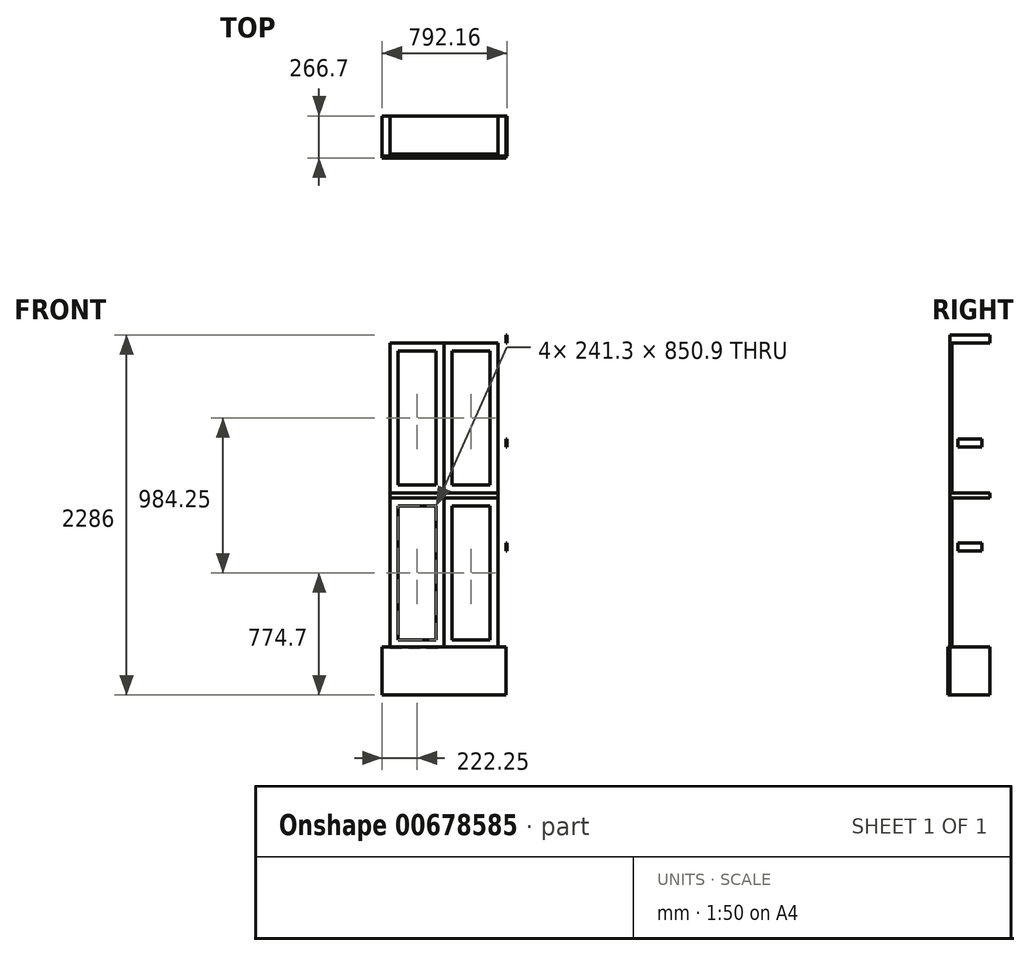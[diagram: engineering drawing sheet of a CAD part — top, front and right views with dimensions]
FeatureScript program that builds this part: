
annotation { "Feature Type Name" : "Feature", "Feature Type Description" : "" }
export const myFeature = defineFeature(function(context is Context, id is Id, definition is map)
    precondition{}
    {
        {
            var Q0;
            Q0=qCreatedBy(makeId("Front.planeOp"),FACE);
            var sketch = newSketch(context, id + "F0", { "sketchPlane" : qUnion([Q0])});
            skLineSegment(sketch, "E0.bottom", {"start": v(393.7, 152.4) * mm, "end": v(-393.7, 152.4) * mm});
            skLineSegment(sketch, "E0.top", {"start": v(393.7, -152.4) * mm, "end": v(-393.7, -152.4) * mm});
            skLineSegment(sketch, "E0.left", {"start": v(393.7, 152.4) * mm, "end": v(393.7, -152.4) * mm});
            skLineSegment(sketch, "E0.right", {"start": v(-393.7, 152.4) * mm, "end": v(-393.7, -152.4) * mm});
            skPoint(sketch, "E0.middle", {"position": v(0, 0) * mm});
            skLineSegment(sketch, "E1.bottom", {"start": v(-393.7, 152.4) * mm, "end": v(-342.9, 152.4) * mm});
            skLineSegment(sketch, "E1.top", {"start": v(-393.7, 2133.6) * mm, "end": v(-342.9, 2133.6) * mm});
            skLineSegment(sketch, "E1.left", {"start": v(-393.7, 152.4) * mm, "end": v(-393.7, 2133.6) * mm});
            skLineSegment(sketch, "E1.right", {"start": v(-342.9, 152.4) * mm, "end": v(-342.9, 2082.8) * mm});
            skLineSegment(sketch, "E2.bottom", {"start": v(393.7, 152.4) * mm, "end": v(342.9, 152.4) * mm});
            skLineSegment(sketch, "E2.top", {"start": v(393.7, 2133.6) * mm, "end": v(342.9, 2133.6) * mm});
            skLineSegment(sketch, "E2.left", {"start": v(393.7, 152.4) * mm, "end": v(393.7, 2133.6) * mm});
            skLineSegment(sketch, "E2.right", {"start": v(342.9, 152.4) * mm, "end": v(342.9, 2082.8) * mm});
            skLineSegment(sketch, "E3.bottom", {"start": v(-393.7, 2133.6) * mm, "end": v(393.7, 2133.6) * mm});
            skLineSegment(sketch, "E3.top", {"start": v(-393.7, 2082.8) * mm, "end": v(393.7, 2082.8) * mm});
            skLineSegment(sketch, "E3.left", {"start": v(-393.7, 2133.6) * mm, "end": v(-393.7, 2082.8) * mm});
            skLineSegment(sketch, "E3.right", {"start": v(393.7, 2133.6) * mm, "end": v(393.7, 2082.8) * mm});
            skLineSegment(sketch, "E4.bottom", {"start": v(-342.9, 1130.3) * mm, "end": v(342.9, 1130.3) * mm});
            skLineSegment(sketch, "E4.top", {"start": v(-342.9, 1098.55) * mm, "end": v(342.9, 1098.55) * mm});
            skLineSegment(sketch, "E4.left", {"start": v(-342.9, 1130.3) * mm, "end": v(-342.9, 1098.55) * mm});
            skLineSegment(sketch, "E4.right", {"start": v(342.9, 1130.3) * mm, "end": v(342.9, 1098.55) * mm});
            skSolve(sketch);
        }
        {
            var Q0;
            {var subQ4=sQuery(id+"F0.wireOp",EDGE,"E3.left");Q0=makeQuery(id+"F0.imprint","IMPRINT",FACE,{"disambiguationData":[TD([[makeQuery(id+"F0.imprint","IMPRINT",EDGE,{"derivedFrom":subQ4}),1.0]])]});}
            var Q1;
            Q1=makeQuery(id+"F0.imprint","IMPRINT",FACE,{"disambiguationData":[TD([[makeQuery(id+"F0.imprint","IMPRINT",EDGE,{"derivedFrom":sQuery(id+"F0.wireOp",EDGE,"E4.bottom")}),-1.0]])]});
            var Q2;
            {var subQ4=sQuery(id+"F0.wireOp",EDGE,"E1.bottom");Q2=makeQuery(id+"F0.imprint","IMPRINT",FACE,{"disambiguationData":[TD([[makeQuery(id+"F0.imprint","IMPRINT",EDGE,{"derivedFrom":subQ4}),1.0]])]});}
            var Q3;
            {var subQ4=sQuery(id+"F0.wireOp",EDGE,"E2.bottom");Q3=makeQuery(id+"F0.imprint","IMPRINT",FACE,{"disambiguationData":[TD([[makeQuery(id+"F0.imprint","IMPRINT",EDGE,{"derivedFrom":subQ4}),-1.0]])]});}
            var Q4;
            Q4=makeQuery(id+"F0.imprint","IMPRINT",FACE,{"disambiguationData":[TD([[makeQuery(id+"F0.imprint","IMPRINT",EDGE,{"derivedFrom":sQuery(id+"F0.wireOp",EDGE,"E0.bottom")}),1.0]])]});
            extrude(context, id + "F1", {"entities" : qUnion([Q0, Q1, Q2, Q3, Q4]), "depth" : 254 * mm, "offsetDistance" : 25.4 * mm});
        }
        {
            var Q0;
            Q0=makeQuery(id+"F1.opExtrude","SWEPT_FACE",FACE,{"disambiguationData":[OSD([sQuery(id+"F0.wireOp",EDGE,"E0.left"),sQuery(id+"F0.wireOp",EDGE,"E2.left"),sQuery(id+"F0.wireOp",EDGE,"E3.right")])]});
            var sketch = newSketch(context, id + "F2", { "sketchPlane" : qUnion([Q0])});
            skLineSegment(sketch, "E5.bottom", {"start": v(-254, 2133.6) * mm, "end": v(0, 2133.6) * mm});
            skLineSegment(sketch, "E5.top", {"start": v(-254, 2082.8) * mm, "end": v(0, 2082.8) * mm});
            skLineSegment(sketch, "E5.left", {"start": v(-254, 2133.6) * mm, "end": v(-254, 2082.8) * mm});
            skLineSegment(sketch, "E5.right", {"start": v(0, 2133.6) * mm, "end": v(0, 2082.8) * mm});
            skLineSegment(sketch, "E6.bottom", {"start": v(-254, 2082.8) * mm, "end": v(-203.2, 2082.8) * mm});
            skLineSegment(sketch, "E6.left", {"start": v(-254, 2082.8) * mm, "end": v(-254, -50.8) * mm});
            skLineSegment(sketch, "E6.right", {"start": v(-203.2, 2082.8) * mm, "end": v(-203.2, 152.4) * mm});
            skLineSegment(sketch, "E7.bottom", {"start": v(0, 2082.8) * mm, "end": v(-50.8, 2082.8) * mm});
            skLineSegment(sketch, "E7.top", {"start": v(0, 82.55) * mm, "end": v(-50.8, 82.55) * mm});
            skLineSegment(sketch, "E7.left", {"start": v(0, 2082.8) * mm, "end": v(0, 82.55) * mm});
            skLineSegment(sketch, "E7.right", {"start": v(-50.8, 2082.8) * mm, "end": v(-50.8, 152.4) * mm});
            skLineSegment(sketch, "E8.bottom", {"start": v(-254, -152.4) * mm, "end": v(0, -152.4) * mm});
            skLineSegment(sketch, "E8.top", {"start": v(-254, 82.55) * mm, "end": v(0, 82.55) * mm});
            skLineSegment(sketch, "E8.left", {"start": v(-254, -152.4) * mm, "end": v(-254, 82.55) * mm});
            skLineSegment(sketch, "E8.right", {"start": v(0, -152.4) * mm, "end": v(0, 82.55) * mm});
            skLineSegment(sketch, "E9.top", {"start": v(-254, 152.4) * mm, "end": v(0, 152.4) * mm});
            skLineSegment(sketch, "E9.left", {"start": v(-254, -50.8) * mm, "end": v(-254, 152.4) * mm});
            skLineSegment(sketch, "E9.right", {"start": v(0, -50.8) * mm, "end": v(0, 152.4) * mm});
            skLineSegment(sketch, "E10.bottom", {"start": v(-203.2, 812.8) * mm, "end": v(-50.8, 812.8) * mm});
            skLineSegment(sketch, "E10.top", {"start": v(-203.2, 762) * mm, "end": v(-50.8, 762) * mm});
            skLineSegment(sketch, "E10.left", {"start": v(-203.2, 812.8) * mm, "end": v(-203.2, 762) * mm});
            skLineSegment(sketch, "E10.right", {"start": v(-50.8, 812.8) * mm, "end": v(-50.8, 762) * mm});
            skLineSegment(sketch, "E11.bottom", {"start": v(-203.2, 1473.2) * mm, "end": v(-50.8, 1473.2) * mm});
            skLineSegment(sketch, "E11.top", {"start": v(-203.2, 1422.4) * mm, "end": v(-50.8, 1422.4) * mm});
            skLineSegment(sketch, "E11.left", {"start": v(-203.2, 1473.2) * mm, "end": v(-203.2, 1422.4) * mm});
            skLineSegment(sketch, "E11.right", {"start": v(-50.8, 1473.2) * mm, "end": v(-50.8, 1422.4) * mm});
            skLineSegment(sketch, "E12.left", {"start": v(-254, 152.4) * mm, "end": v(-254, 82.55) * mm});
            skLineSegment(sketch, "E12.right", {"start": v(0, 152.4) * mm, "end": v(0, 82.55) * mm});
            skSolve(sketch);
        }
        {
            var Q0;
            Q0=makeQuery(id+"F2.imprint","IMPRINT",FACE,{"disambiguationData":[TD([[makeQuery(id+"F2.imprint","IMPRINT",EDGE,{"derivedFrom":sQuery(id+"F2.wireOp",EDGE,"E5.bottom")}),-1.0]])]});
            var Q1;
            {var subQ3=sQuery(id+"F2.wireOp",EDGE,"E6.bottom");Q1=makeQuery(id+"F2.imprint","IMPRINT",FACE,{"disambiguationData":[TD([[makeQuery(id+"F2.imprint","IMPRINT",EDGE,{"derivedFrom":subQ3}),-1.0]])]});}
            var Q2;
            {var subQ3=sQuery(id+"F2.wireOp",EDGE,"E7.bottom");Q2=makeQuery(id+"F2.imprint","IMPRINT",FACE,{"disambiguationData":[TD([[makeQuery(id+"F2.imprint","IMPRINT",EDGE,{"derivedFrom":subQ3}),1.0]])]});}
            var Q3;
            {var subQ0=sQuery(id+"F2.wireOp",EDGE,"E12.left");Q3=makeQuery(id+"F2.imprint","IMPRINT",FACE,{"disambiguationData":[TD([[makeQuery(id+"F2.imprint","IMPRINT",EDGE,{"derivedFrom":subQ0}),1.0]])]});}
            var Q4;
            Q4=makeQuery(id+"F2.imprint","IMPRINT",FACE,{"disambiguationData":[TD([[makeQuery(id+"F2.imprint","IMPRINT",EDGE,{"derivedFrom":sQuery(id+"F2.wireOp",EDGE,"E10.bottom")}),-1.0]])]});
            var Q5;
            Q5=makeQuery(id+"F2.imprint","IMPRINT",FACE,{"disambiguationData":[TD([[makeQuery(id+"F2.imprint","IMPRINT",EDGE,{"derivedFrom":sQuery(id+"F2.wireOp",EDGE,"E11.bottom")}),-1.0]])]});
            extrude(context, id + "F3", {"entities" : qUnion([Q0, Q1, Q2, Q3, Q4, Q5]), "operationType" : NewBodyOperationType.ADD, "depth" : 4.76 * mm, "offsetDistance" : 25.4 * mm});
        }
        {
            var Q0;
            Q0=makeQuery(id+"F3.boolean.opBoolean","MERGE",FACE,{"derivedFrom":[makeQuery(id+"F1.opExtrude","CAP_FACE",FACE,{"disambiguationData":[OSD([sQuery(id+"F0.wireOp",EDGE,"E0.bottom"),sQuery(id+"F0.wireOp",EDGE,"E0.top"),sQuery(id+"F0.wireOp",EDGE,"E0.left"),sQuery(id+"F0.wireOp",EDGE,"E0.right"),sQuery(id+"F0.wireOp",EDGE,"E1.left"),sQuery(id+"F0.wireOp",EDGE,"E1.right"),sQuery(id+"F0.wireOp",EDGE,"E2.left"),sQuery(id+"F0.wireOp",EDGE,"E2.right"),sQuery(id+"F0.wireOp",EDGE,"E3.bottom"),sQuery(id+"F0.wireOp",EDGE,"E3.top"),sQuery(id+"F0.wireOp",EDGE,"E3.left"),sQuery(id+"F0.wireOp",EDGE,"E3.right"),sQuery(id+"F0.wireOp",EDGE,"E4.bottom"),sQuery(id+"F0.wireOp",EDGE,"E4.top")])],"isStart":false}),makeQuery(id+"F3.opExtrude","SWEPT_FACE",FACE,{"disambiguationData":[OSD([sQuery(id+"F2.wireOp",EDGE,"E5.left"),sQuery(id+"F2.wireOp",EDGE,"E6.left"),sQuery(id+"F2.wireOp",EDGE,"E12.left")])]})]});
            var sketch = newSketch(context, id + "F4", { "sketchPlane" : qUnion([Q0])});
            skLineSegment(sketch, "E13.bottom", {"start": v(-342.9, 2082.8) * mm, "end": v(0, 2082.8) * mm});
            skLineSegment(sketch, "E13.top", {"start": v(-342.9, 1130.3) * mm, "end": v(0, 1130.3) * mm});
            skLineSegment(sketch, "E13.left", {"start": v(-342.9, 2082.8) * mm, "end": v(-342.9, 1130.3) * mm});
            skLineSegment(sketch, "E13.right", {"start": v(0, 2082.8) * mm, "end": v(0, 1130.3) * mm});
            skLineSegment(sketch, "E14.0", {"start": v(-292.1, 2032) * mm, "end": v(-50.8, 2032) * mm});
            skLineSegment(sketch, "E14.1", {"start": v(-292.1, 2032) * mm, "end": v(-292.1, 1181.1) * mm});
            skLineSegment(sketch, "E14.2", {"start": v(-292.1, 1181.1) * mm, "end": v(-50.8, 1181.1) * mm});
            skLineSegment(sketch, "E14.3", {"start": v(-50.8, 2032) * mm, "end": v(-50.8, 1181.1) * mm});
            skLineSegment(sketch, "E15", {"start": v(0, 2320.6) * mm, "end": v(0, 2133.6) * mm, "construction": true});
            skSolve(sketch);
        }
        {
            var Q0;
            Q0=makeQuery(id+"F4.imprint","IMPRINT",FACE,{"disambiguationData":[TD([[makeQuery(id+"F4.imprint","IMPRINT",EDGE,{"derivedFrom":sQuery(id+"F4.wireOp",EDGE,"E13.bottom")}),-1.0]])]});
            extrude(context, id + "F5", {"entities" : qUnion([Q0]), "oppositeDirection" : true, "depth" : 12.7 * mm, "offsetDistance" : 25.4 * mm});
        }
        {
            var Q0;
            Q0=makeQuery(id+"F5.opExtrude","SWEPT_FACE",FACE,{"disambiguationData":[OSD([sQuery(id+"F4.wireOp",EDGE,"E13.right")])]});
            var sketch = newSketch(context, id + "F6", { "sketchPlane" : qUnion([Q0])});
            skSolve(sketch);
        }
        {
            var Q0;
            Q0=makeQuery(id+"F5.opExtrude","SWEPT_BODY",BODY,{"disambiguationData":[OSD([sQuery(id+"F4.wireOp",EDGE,"E13.bottom"),sQuery(id+"F4.wireOp",EDGE,"E13.top"),sQuery(id+"F4.wireOp",EDGE,"E13.left"),sQuery(id+"F4.wireOp",EDGE,"E13.right"),sQuery(id+"F4.wireOp",EDGE,"E14.0"),sQuery(id+"F4.wireOp",EDGE,"E14.1"),sQuery(id+"F4.wireOp",EDGE,"E14.2"),sQuery(id+"F4.wireOp",EDGE,"E14.3")])]});
            var Q1;
            {var subQ0=sQuery(id+"F4.wireOp",EDGE,"E13.right");Q1=makeQuery(id+"F6.imprint","IMPRINT",FACE,{"disambiguationData":[TD([[makeQuery(id+"F6.imprint","IMPRINT",EDGE,{"derivedFrom":makeQuery(id+"F5.opExtrude","CAP_EDGE",EDGE,{"disambiguationData":[OSD([subQ0])],"isStart":true})}),1.0]])]});}
            mirror(context, id + "F7", {"entities" : qUnion([Q0]), "mirrorPlane" : qUnion([Q1])});
        }
        {
            var Q0;
            Q0=makeQuery(id+"F1.opExtrude","SWEPT_FACE",FACE,{"disambiguationData":[OSD([sQuery(id+"F0.wireOp",EDGE,"E4.bottom")])]});
            cPlane(context, id + "F8", {"entities" : qUnion([Q0]), "cplaneType" : CPlaneType.OFFSET, "offset" : 15.88 * mm, "oppositeDirection" : true, "width" : 152.4 * mm, "height" : 152.4 * mm});
        }
        {
            var Q0;
            Q0=makeQuery(id+"F5.opExtrude","SWEPT_BODY",BODY,{"disambiguationData":[OSD([sQuery(id+"F4.wireOp",EDGE,"E13.bottom"),sQuery(id+"F4.wireOp",EDGE,"E13.top"),sQuery(id+"F4.wireOp",EDGE,"E13.left"),sQuery(id+"F4.wireOp",EDGE,"E13.right"),sQuery(id+"F4.wireOp",EDGE,"E14.0"),sQuery(id+"F4.wireOp",EDGE,"E14.1"),sQuery(id+"F4.wireOp",EDGE,"E14.2"),sQuery(id+"F4.wireOp",EDGE,"E14.3")])]});
            var Q1;
            Q1=makeQuery(id+"F7.opPattern","COPY",BODY,{"derivedFrom":makeQuery(id+"F5.opExtrude","SWEPT_BODY",BODY,{"disambiguationData":[OSD([sQuery(id+"F4.wireOp",EDGE,"E13.bottom"),sQuery(id+"F4.wireOp",EDGE,"E13.top"),sQuery(id+"F4.wireOp",EDGE,"E13.left"),sQuery(id+"F4.wireOp",EDGE,"E13.right"),sQuery(id+"F4.wireOp",EDGE,"E14.0"),sQuery(id+"F4.wireOp",EDGE,"E14.1"),sQuery(id+"F4.wireOp",EDGE,"E14.2"),sQuery(id+"F4.wireOp",EDGE,"E14.3")])]}),"instanceName":"1"});
            var Q2;
            Q2=qCreatedBy(id+"F8.planeOp",FACE);
            mirror(context, id + "F9", {"entities" : qUnion([Q0, Q1]), "mirrorPlane" : qUnion([Q2])});
        }
        {
            var Q0;
            Q0=makeQuery(id+"F3.boolean.opBoolean","MERGE",FACE,{"derivedFrom":[makeQuery(id+"F1.opExtrude","CAP_FACE",FACE,{"disambiguationData":[OSD([sQuery(id+"F0.wireOp",EDGE,"E0.bottom"),sQuery(id+"F0.wireOp",EDGE,"E0.top"),sQuery(id+"F0.wireOp",EDGE,"E0.left"),sQuery(id+"F0.wireOp",EDGE,"E0.right"),sQuery(id+"F0.wireOp",EDGE,"E1.left"),sQuery(id+"F0.wireOp",EDGE,"E1.right"),sQuery(id+"F0.wireOp",EDGE,"E2.left"),sQuery(id+"F0.wireOp",EDGE,"E2.right"),sQuery(id+"F0.wireOp",EDGE,"E3.bottom"),sQuery(id+"F0.wireOp",EDGE,"E3.top"),sQuery(id+"F0.wireOp",EDGE,"E3.left"),sQuery(id+"F0.wireOp",EDGE,"E3.right"),sQuery(id+"F0.wireOp",EDGE,"E4.bottom"),sQuery(id+"F0.wireOp",EDGE,"E4.top")])],"isStart":false}),makeQuery(id+"F3.opExtrude","SWEPT_FACE",FACE,{"disambiguationData":[OSD([sQuery(id+"F2.wireOp",EDGE,"E5.left"),sQuery(id+"F2.wireOp",EDGE,"E6.left"),sQuery(id+"F2.wireOp",EDGE,"E12.left")])]})]});
            var sketch = newSketch(context, id + "F10", { "sketchPlane" : qUnion([Q0])});
            skLineSegment(sketch, "E16.bottom", {"start": v(-393.7, -152.4) * mm, "end": v(398.46, -152.4) * mm});
            skLineSegment(sketch, "E16.top", {"start": v(-393.7, 152.4) * mm, "end": v(398.46, 152.4) * mm});
            skLineSegment(sketch, "E16.left", {"start": v(-393.7, -152.4) * mm, "end": v(-393.7, 152.4) * mm});
            skLineSegment(sketch, "E16.right", {"start": v(398.46, -152.4) * mm, "end": v(398.46, 152.4) * mm});
            skSolve(sketch);
        }
        {
            var Q0;
            {var subQ10=sQuery(id+"F10.wireOp",EDGE,"E16.left");Q0=makeQuery(id+"F10.imprint","IMPRINT",FACE,{"disambiguationData":[TD([[makeQuery(id+"F10.imprint","IMPRINT",EDGE,{"derivedFrom":subQ10}),1.0]])]});}
            extrude(context, id + "F11", {"entities" : qUnion([Q0]), "depth" : 12.7 * mm, "offsetDistance" : 25.4 * mm});
        }
    });
